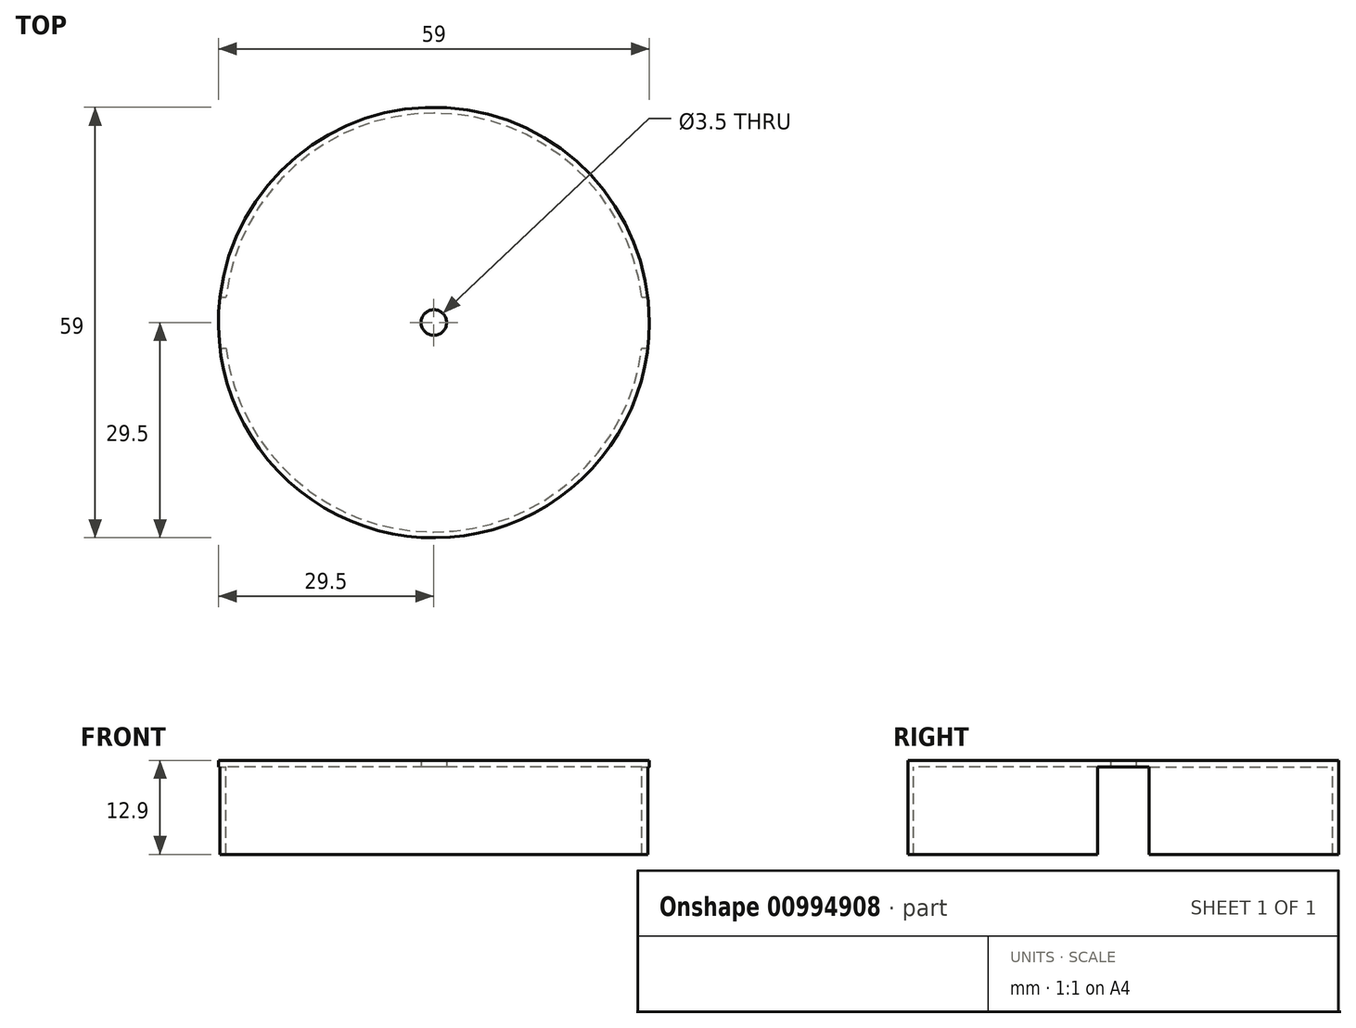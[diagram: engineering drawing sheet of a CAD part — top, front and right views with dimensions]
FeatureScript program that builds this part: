
annotation { "Feature Type Name" : "Feature", "Feature Type Description" : "" }
export const myFeature = defineFeature(function(context is Context, id is Id, definition is map)
    precondition{}
    {
        {
            var Q0;
            Q0=qCreatedBy(makeId("Top.planeOp"),FACE);
            var sketch = newSketch(context, id + "F0", { "sketchPlane" : qUnion([Q0])});
            skCircle(sketch, "E0", {"center": v(0, 0) * mm, "radius": 29.5 * mm});
            skCircle(sketch, "E1", {"center": v(0, 0) * mm, "radius": 1.75 * mm});
            skSolve(sketch);
        }
        {
            var Q0;
            Q0 = qSketchRegion(id + "F0", true);
            extrude(context, id + "F1", {"entities" : qUnion([Q0]), "depth" : 0.9 * mm, "offsetDistance" : 25 * mm});
        }
        {
            var Q0;
            Q0=makeQuery(id+"F1.opExtrude","CAP_FACE",FACE,{"disambiguationData":[OSD([sQuery(id+"F0.wireOp",EDGE,"E0")])],"isStart":true});
            var sketch = newSketch(context, id + "F2", { "sketchPlane" : qUnion([Q0])});
            skCircle(sketch, "E2.0", {"center": v(0, 0) * mm, "radius": 29.5 * mm});
            skCircle(sketch, "E3.0", {"center": v(0, 0) * mm, "radius": 28.7 * mm});
            skSolve(sketch);
        }
        {
            var Q0;
            Q0 = qSketchRegion(id + "F2", true);
            extrude(context, id + "F3", {"entities" : qUnion([Q0]), "operationType" : NewBodyOperationType.ADD, "depth" : 12 * mm, "offsetDistance" : 25 * mm});
        }
        {
            var Q0;
            Q0=makeQuery(id+"F3.opExtrude","CAP_FACE",FACE,{"disambiguationData":[OSD([sQuery(id+"F2.wireOp",EDGE,"E2.0"),sQuery(id+"F2.wireOp",EDGE,"E3.0")])],"isStart":false});
            var sketch = newSketch(context, id + "F4", { "sketchPlane" : qUnion([Q0])});
            skLineSegment(sketch, "E4.bottom", {"start": v(-29.5, 3.5) * mm, "end": v(29.5, 3.5) * mm});
            skLineSegment(sketch, "E4.top", {"start": v(-29.5, -3.5) * mm, "end": v(29.5, -3.5) * mm});
            skLineSegment(sketch, "E4.left", {"start": v(-29.5, 3.5) * mm, "end": v(-29.5, -3.5) * mm});
            skLineSegment(sketch, "E4.right", {"start": v(29.5, 3.5) * mm, "end": v(29.5, -3.5) * mm});
            skPoint(sketch, "E4.middle", {"position": v(0, 0) * mm});
            skSolve(sketch);
        }
        {
            var Q0;
            Q0 = qSketchRegion(id + "F4", true);
            var Q1;
            Q1=makeQuery(id+"F1.opExtrude","CAP_FACE",FACE,{"disambiguationData":[OSD([sQuery(id+"F0.wireOp",EDGE,"E0"),sQuery(id+"F0.wireOp",EDGE,"E1")])],"isStart":true});
            extrude(context, id + "F5", {"entities" : qUnion([Q0]), "operationType" : NewBodyOperationType.REMOVE, "endBound" : BoundingType.UP_TO_SURFACE, "oppositeDirection" : true, "depth" : 25 * mm, "endBoundEntityFace" : qUnion([Q1]), "offsetDistance" : 25 * mm});
        }
    });
